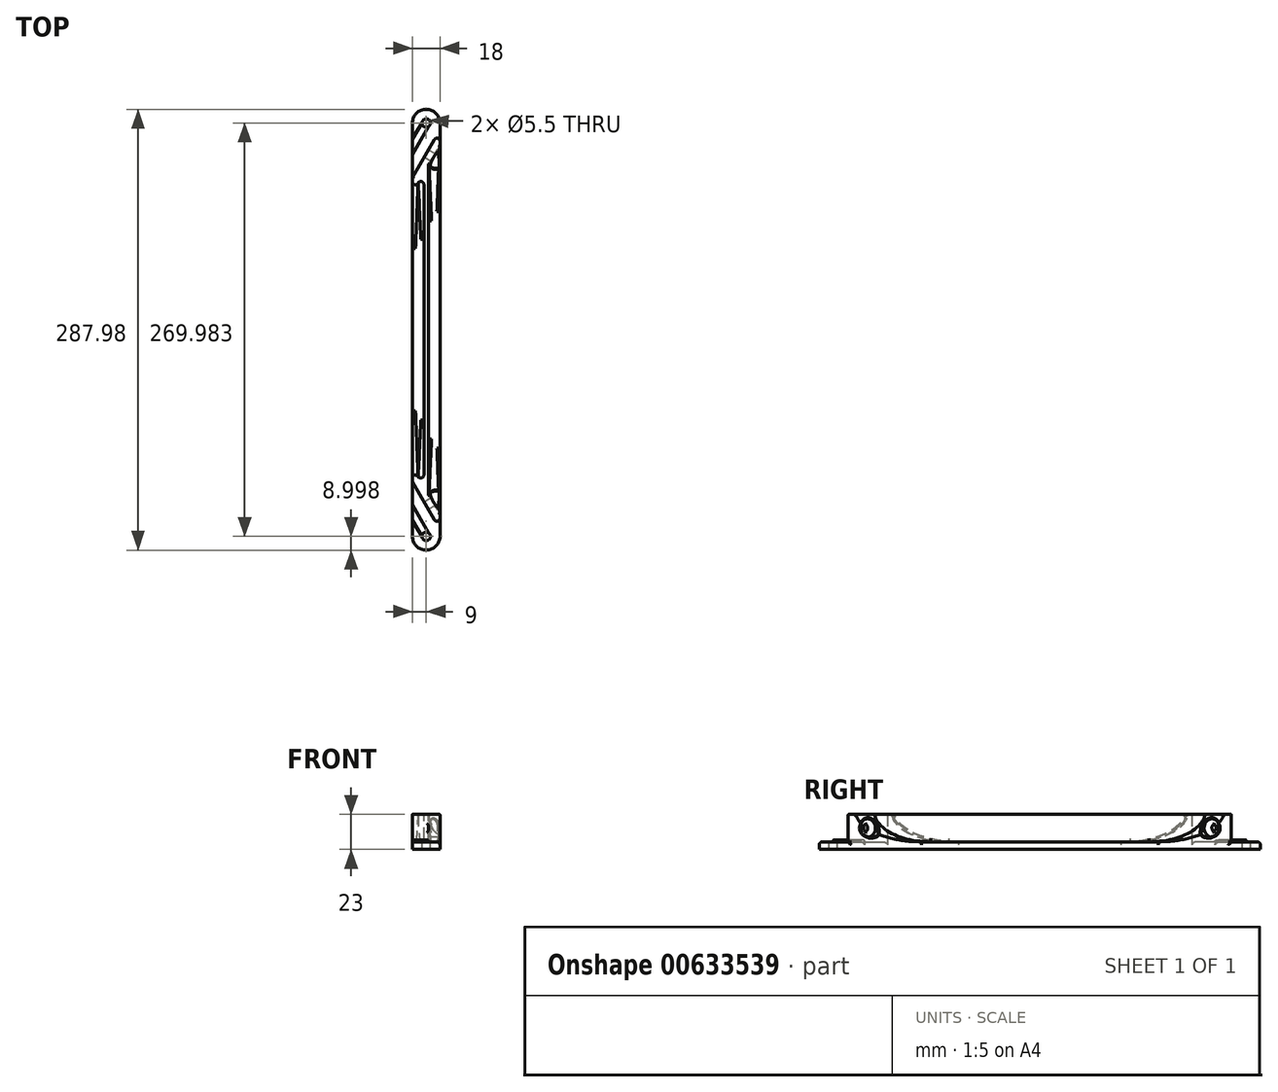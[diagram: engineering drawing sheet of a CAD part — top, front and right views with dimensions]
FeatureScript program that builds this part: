
annotation { "Feature Type Name" : "Feature", "Feature Type Description" : "" }
export const myFeature = defineFeature(function(context is Context, id is Id, definition is map)
    precondition{}
    {
        {
            var Q0;
            Q0=qCreatedBy(makeId("Top.planeOp"),FACE);
            var sketch = newSketch(context, id + "F0", { "sketchPlane" : qUnion([Q0])});
            skLineSegment(sketch, "E0.top", {"start": v(9, 135) * mm, "end": v(-9, 135) * mm, "construction": true});
            skPoint(sketch, "E0.middle", {"position": v(0, 0) * mm});
            skArc(sketch, "E1", {"start": v(-9, 135) * mm, "mid": v(0, 144) * mm, "end": v(9, 135) * mm});
            skCircle(sketch, "E2", {"center": v(0, 135) * mm, "radius": 2.75 * mm});
            skCircle(sketch, "E3", {"center": v(0, 135) * mm, "radius": 2.5 * mm, "construction": true});
            skLineSegment(sketch, "E4", {"start": v(-9.23, 124) * mm, "end": v(2.16, 143.73) * mm});
            skLineSegment(sketch, "E5", {"start": v(-9.23, 114) * mm, "end": v(6.49, 141.23) * mm});
            skCircle(sketch, "E6", {"center": v(0, 135) * mm, "radius": 15 * mm, "construction": true});
            skLineSegment(sketch, "E7.MirrorCS", {"start": v(9, 135) * mm, "end": v(9, 0) * mm});
            skLineSegment(sketch, "E8.MirrorCS", {"start": v(-9, 135) * mm, "end": v(-9, 0) * mm});
            skLineSegment(sketch, "E9", {"start": v(9, 130.58) * mm, "end": v(-9, 99.4) * mm});
            skLineSegment(sketch, "E10", {"start": v(9, 120.58) * mm, "end": v(-9, 89.4) * mm});
            skLineSegment(sketch, "E11", {"start": v(-1.5, 102.4) * mm, "end": v(-1.5, 0) * mm});
            skCircle(sketch, "E12", {"center": v(0, 0) * mm, "radius": 1.5 * mm, "construction": true});
            skLineSegment(sketch, "E13", {"start": v(1.5, 107.59) * mm, "end": v(1.5, 0) * mm});
            skLineSegment(sketch, "E14", {"start": v(-9, 0) * mm, "end": v(9, 0) * mm});
            skCircle(sketch, "E15", {"center": v(1.5, 0) * mm, "radius": 150 * mm, "construction": true});
            skSolve(sketch);
        }
        {
            var Q0;
            Q0=qSketchRegion(id+"F0",true);
            var Q1;
            {var subQ0=sQuery(id+"F0.wireOp",EDGE,"E11");Q1=makeQuery(id+"F0.imprint","IMPRINT",FACE,{"disambiguationData":[TD([[makeQuery(id+"F0.imprint","IMPRINT",EDGE,{"derivedFrom":subQ0}),1.0]])]});}
            extrude(context, id + "F1", {"entities" : qUnion([Q0, Q1]), "oppositeDirection" : true, "depth" : 5 * mm, "offsetDistance" : 25 * mm});
        }
        {
            var Q0;
            {var subQ0=sQuery(id+"F0.wireOp",EDGE,"E4");var subQ1=sQuery(id+"F0.wireOp",EDGE,"E2");var subQ2=makeQuery(id+"F0.imprint","INTERSECT",VERTEX,{"disambiguationData":[OD(0.0)],"derivedFrom":[subQ1,subQ0]});Q0=makeQuery(id+"F0.imprint","IMPRINT",FACE,{"disambiguationData":[TD([[makeQuery(id+"F0.imprint","IMPRINT",EDGE,{"disambiguationData":[TD([[subQ2,-1.0]])],"derivedFrom":subQ1}),-1.0]])]});}
            var Q1;
            {var subQ0=sQuery(id+"F0.wireOp",EDGE,"E4");var subQ1=sQuery(id+"F0.wireOp",EDGE,"E1");var subQ2=makeQuery(id+"F0.imprint","INTERSECT",VERTEX,{"derivedFrom":[subQ1,subQ0]});Q1=makeQuery(id+"F0.imprint","IMPRINT",FACE,{"disambiguationData":[TD([[makeQuery(id+"F0.imprint","IMPRINT",EDGE,{"disambiguationData":[TD([[subQ2,-1.0]])],"derivedFrom":subQ1}),-1.0]])]});}
            var Q2;
            {var subQ0=sQuery(id+"F0.wireOp",EDGE,"3b4f7be5-a3c5-4cc3-b924-c977956cb13f3.MirrorCS");var subQ1=sQuery(id+"F0.wireOp",EDGE,"3b4f7be5-a3c5-4cc3-b924-c977956cb13f0.MirrorC");var subQ2=makeQuery(id+"F0.imprint","INTERSECT",VERTEX,{"disambiguationData":[OD(0.0)],"derivedFrom":[subQ1,subQ0]});Q2=makeQuery(id+"F0.imprint","IMPRINT",FACE,{"disambiguationData":[TD([[makeQuery(id+"F0.imprint","IMPRINT",EDGE,{"disambiguationData":[TD([[subQ2,-1.0]])],"derivedFrom":subQ1}),1.0]])]});}
            var Q3;
            {var subQ0=sQuery(id+"F0.wireOp",EDGE,"3b4f7be5-a3c5-4cc3-b924-c977956cb13f3.MirrorCS");var subQ1=sQuery(id+"F0.wireOp",EDGE,"3b4f7be5-a3c5-4cc3-b924-c977956cb13f0.MirrorC");var subQ2=makeQuery(id+"F0.imprint","INTERSECT",VERTEX,{"disambiguationData":[OD(1.0)],"derivedFrom":[subQ1,subQ0]});Q3=makeQuery(id+"F0.imprint","IMPRINT",FACE,{"disambiguationData":[TD([[makeQuery(id+"F0.imprint","IMPRINT",EDGE,{"disambiguationData":[TD([[subQ2,1.0]])],"derivedFrom":subQ1}),1.0]])]});}
            extrude(context, id + "F2", {"entities" : qUnion([Q0, Q1, Q2, Q3]), "operationType" : NewBodyOperationType.ADD, "depth" : 1.2 * mm, "offsetDistance" : 25 * mm});
        }
        {
            var Q0;
            {var subQ0=sQuery(id+"F0.wireOp",EDGE,"E9");Q0=makeQuery(id+"F0.imprint","IMPRINT",FACE,{"disambiguationData":[TD([[makeQuery(id+"F0.imprint","IMPRINT",EDGE,{"derivedFrom":subQ0}),1.0]])]});}
            var Q1;
            {var subQ0=sQuery(id+"F0.wireOp",EDGE,"52fd9cd9-2778-4df9-a2e4-210ae1353c010.MirrorCS");Q1=makeQuery(id+"F0.imprint","IMPRINT",FACE,{"disambiguationData":[TD([[makeQuery(id+"F0.imprint","IMPRINT",EDGE,{"derivedFrom":subQ0}),-1.0]])]});}
            var Q2;
            {var subQ0=sQuery(id+"F0.wireOp",EDGE,"E11");Q2=makeQuery(id+"F0.imprint","IMPRINT",FACE,{"disambiguationData":[TD([[makeQuery(id+"F0.imprint","IMPRINT",EDGE,{"derivedFrom":subQ0}),1.0]])]});}
            extrude(context, id + "F3", {"entities" : qUnion([Q0, Q1, Q2]), "operationType" : NewBodyOperationType.ADD, "depth" : 18 * mm, "offsetDistance" : 25 * mm});
        }
        {
            var Q0;
            {var subQ0=sQuery(id+"F0.wireOp",EDGE,"E10");Q0=makeQuery(id+"F3.opExtrude","CAP_EDGE",EDGE,{"disambiguationData":[OSD([subQ0]),TDD([makeQuery(id+"F0.imprint","IMPRINT",EDGE,{"disambiguationData":[TD([[makeQuery(id+"F0.imprint","INTERSECT",VERTEX,{"derivedFrom":[sQuery(id+"F0.wireOp",EDGE,"E8.MirrorCS"),subQ0]}),1.0]])],"derivedFrom":subQ0})])],"isStart":true});}
            var Q1;
            {var subQ0=sQuery(id+"F0.wireOp",EDGE,"E10");Q1=makeQuery(id+"F3.opExtrude","CAP_EDGE",EDGE,{"disambiguationData":[OSD([subQ0]),TDD([makeQuery(id+"F0.imprint","IMPRINT",EDGE,{"disambiguationData":[TD([[makeQuery(id+"F0.imprint","INTERSECT",VERTEX,{"derivedFrom":[sQuery(id+"F0.wireOp",EDGE,"E7.MirrorCS"),subQ0]}),-1.0]])],"derivedFrom":subQ0})])],"isStart":true});}
            fillet(context, id + "F4", {"entities" : qUnion([Q0, Q1]), "radius" : 20 * mm, "tangentPropagation" : true, "allowEdgeOverflow" : false});
        }
        {
            var Q0;
            Q0=makeQuery(id+"F3.opExtrude","SWEPT_FACE",FACE,{"disambiguationData":[OSD([sQuery(id+"F0.wireOp",EDGE,"E9")])]});
            var sketch = newSketch(context, id + "F5", { "sketchPlane" : qUnion([Q0])});
            skCircle(sketch, "E16", {"center": v(-99.59, 9) * mm, "radius": 2.75 * mm});
            skCircle(sketch, "E17", {"center": v(-99.59, 9) * mm, "radius": 6 * mm});
            skSolve(sketch);
        }
        {
            var Q0;
            Q0=makeQuery(id+"F5.imprint","IMPRINT",FACE,{"disambiguationData":[TD([[makeQuery(id+"F5.imprint","IMPRINT",EDGE,{"derivedFrom":sQuery(id+"F5.wireOp",EDGE,"E16")}),-1.0]])]});
            var Q1;
            Q1=makeQuery(id+"F5.imprint","IMPRINT",FACE,{"disambiguationData":[TD([[makeQuery(id+"F5.imprint","IMPRINT",EDGE,{"derivedFrom":sQuery(id+"F5.wireOp",EDGE,"E16")}),1.0]])]});
            extrude(context, id + "F6", {"entities" : qUnion([Q0, Q1]), "operationType" : NewBodyOperationType.REMOVE, "oppositeDirection" : true, "depth" : 25 * mm, "offsetDistance" : 25 * mm});
        }
        {
            var Q0;
            Q0=makeQuery(id+"F5.imprint","IMPRINT",FACE,{"disambiguationData":[TD([[makeQuery(id+"F5.imprint","IMPRINT",EDGE,{"derivedFrom":sQuery(id+"F5.wireOp",EDGE,"E16")}),-1.0]])]});
            extrude(context, id + "F7", {"entities" : qUnion([Q0]), "operationType" : NewBodyOperationType.ADD, "oppositeDirection" : true, "depth" : 5 * mm, "offsetDistance" : 25 * mm});
        }
        {
            var Q0;
            {var subQ0=sQuery(id+"F0.wireOp",EDGE,"E8.MirrorCS");var subQ1=sQuery(id+"F0.wireOp",EDGE,"E10");Q0=makeQuery(id+"F4.opFillet","BLEND_EDGE",EDGE,{"blendedFrom":[makeQuery(id+"F3.opExtrude","CAP_EDGE",EDGE,{"disambiguationData":[OSD([subQ1]),TDD([makeQuery(id+"F0.imprint","IMPRINT",EDGE,{"disambiguationData":[TD([[makeQuery(id+"F0.imprint","INTERSECT",VERTEX,{"derivedFrom":[subQ0,subQ1]}),1.0]])],"derivedFrom":subQ1})])],"isStart":true}),makeQuery(id+"F3.boolean.opBoolean","MERGE",FACE,{"derivedFrom":[makeQuery(id+"F2.boolean.opBoolean","MERGE",FACE,{"derivedFrom":[makeQuery(id+"F1.opExtrude","SWEPT_FACE",FACE,{"disambiguationData":[OSD([subQ0])]}),makeQuery(id+"F2.opExtrude","SWEPT_FACE",FACE,{"disambiguationData":[OSD([subQ0])]})]}),makeQuery(id+"F3.opExtrude","SWEPT_FACE",FACE,{"disambiguationData":[OSD([subQ0])]})]})],"blendedInto":[makeQuery(id+"F3.boolean.opBoolean","MERGE",FACE,{"derivedFrom":[makeQuery(id+"F2.boolean.opBoolean","MERGE",FACE,{"derivedFrom":[makeQuery(id+"F1.opExtrude","SWEPT_FACE",FACE,{"disambiguationData":[OSD([subQ0])]}),makeQuery(id+"F2.opExtrude","SWEPT_FACE",FACE,{"disambiguationData":[OSD([subQ0])]})]}),makeQuery(id+"F3.opExtrude","SWEPT_FACE",FACE,{"disambiguationData":[OSD([subQ0])]})]})]});}
            var Q1;
            Q1=makeQuery(id+"F3.opExtrude","SWEPT_EDGE",EDGE,{"disambiguationData":[OSD([sQuery(id+"F0.wireOp",EDGE,"E7.MirrorCS"),sQuery(id+"F0.wireOp",EDGE,"E9")])]});
            var Q2;
            {var subQ0=sQuery(id+"F0.wireOp",EDGE,"E13");var subQ1=sQuery(id+"F0.wireOp",EDGE,"E10");Q2=makeQuery(id+"F4.opFillet","BLEND_EDGE",EDGE,{"blendedFrom":[makeQuery(id+"F3.opExtrude","CAP_EDGE",EDGE,{"disambiguationData":[OSD([subQ1]),TDD([makeQuery(id+"F0.imprint","IMPRINT",EDGE,{"disambiguationData":[TD([[makeQuery(id+"F0.imprint","INTERSECT",VERTEX,{"derivedFrom":[sQuery(id+"F0.wireOp",EDGE,"E7.MirrorCS"),subQ1]}),-1.0]])],"derivedFrom":subQ1})])],"isStart":true}),makeQuery(id+"F3.opExtrude","SWEPT_FACE",FACE,{"disambiguationData":[OSD([subQ0])]})],"blendedInto":[makeQuery(id+"F3.opExtrude","SWEPT_FACE",FACE,{"disambiguationData":[OSD([subQ0])]})]});}
            var Q3;
            Q3=makeQuery(id+"F3.opExtrude","CAP_EDGE",EDGE,{"disambiguationData":[OSD([sQuery(id+"F0.wireOp",EDGE,"E11")])],"isStart":true});
            var Q4;
            {var subQ0=sQuery(id+"F0.wireOp",EDGE,"E8.MirrorCS");var subQ6=sQuery(id+"F0.wireOp",EDGE,"E14");Q4=makeQuery(id+"F3.boolean.opBoolean","SPLIT",EDGE,{"disambiguationData":[TD([makeQuery(id+"F3.opExtrude","SWEPT_FACE",FACE,{"disambiguationData":[OSD([sQuery(id+"F0.wireOp",EDGE,"E9")])]})])],"derivedFrom":makeQuery(id+"F2.boolean.opBoolean","SPLIT",EDGE,{"disambiguationData":[TD([makeQuery(id+"F1.opExtrude","SWEPT_FACE",FACE,{"disambiguationData":[OSD([subQ6])]})])],"derivedFrom":makeQuery(id+"F1.opExtrude","CAP_EDGE",EDGE,{"disambiguationData":[OSD([subQ0])],"isStart":true})})});}
            var Q5;
            {var subQ0=sQuery(id+"F0.wireOp",EDGE,"E1");var subQ1=sQuery(id+"F0.wireOp",EDGE,"E8.MirrorCS");Q5=makeQuery(id+"F2.boolean.opBoolean","SPLIT",EDGE,{"disambiguationData":[TD([makeQuery(id+"F1.opExtrude","SWEPT_FACE",FACE,{"disambiguationData":[OSD([subQ0])]})])],"derivedFrom":makeQuery(id+"F1.opExtrude","CAP_EDGE",EDGE,{"disambiguationData":[OSD([subQ1])],"isStart":true})});}
            var Q6;
            {var subQ0=sQuery(id+"F0.wireOp",EDGE,"E7.MirrorCS");var subQ1=sQuery(id+"F0.wireOp",EDGE,"E1");Q6=makeQuery(id+"F2.boolean.opBoolean","SPLIT",EDGE,{"disambiguationData":[TD([makeQuery(id+"F1.opExtrude","SWEPT_FACE",FACE,{"disambiguationData":[OSD([subQ0])]})])],"derivedFrom":makeQuery(id+"F1.opExtrude","CAP_EDGE",EDGE,{"disambiguationData":[OSD([subQ1])],"isStart":true})});}
            var Q7;
            {var subQ0=sQuery(id+"F0.wireOp",EDGE,"E7.MirrorCS");var subQ1=sQuery(id+"F0.wireOp",EDGE,"E14");Q7=makeQuery(id+"F3.boolean.opBoolean","SPLIT",EDGE,{"disambiguationData":[TD([makeQuery(id+"F1.opExtrude","SWEPT_FACE",FACE,{"disambiguationData":[OSD([subQ1])]})])],"derivedFrom":makeQuery(id+"F1.opExtrude","CAP_EDGE",EDGE,{"disambiguationData":[OSD([subQ0])],"isStart":true})});}
            var Q8;
            {var subQ0=sQuery(id+"F0.wireOp",EDGE,"E10");var subQ1=sQuery(id+"F0.wireOp",EDGE,"E7.MirrorCS");var subQ2=sQuery(id+"F0.wireOp",EDGE,"E13");var subQ3=makeQuery(id+"F3.opExtrude","CAP_EDGE",EDGE,{"disambiguationData":[OSD([subQ0]),TDD([makeQuery(id+"F0.imprint","IMPRINT",EDGE,{"disambiguationData":[TD([[makeQuery(id+"F0.imprint","INTERSECT",VERTEX,{"derivedFrom":[subQ1,subQ0]}),-1.0]])],"derivedFrom":subQ0})])],"isStart":true});var subQ4=makeQuery(id+"F3.opExtrude","SWEPT_FACE",FACE,{"disambiguationData":[OSD([subQ1])]});var subQ5=makeQuery(id+"F1.opExtrude","SWEPT_FACE",FACE,{"disambiguationData":[OSD([subQ1])]});Q8=makeQuery(id+"F6.boolean.opBoolean","SPLIT",EDGE,{"disambiguationData":[TD([makeQuery(id+"F3.opExtrude","CAP_FACE",FACE,{"disambiguationData":[OSD([subQ1,sQuery(id+"F0.wireOp",EDGE,"E8.MirrorCS"),sQuery(id+"F0.wireOp",EDGE,"E9"),subQ0,sQuery(id+"F0.wireOp",EDGE,"E11"),subQ2,sQuery(id+"F0.wireOp",EDGE,"E14")])],"isStart":false})])],"derivedFrom":makeQuery(id+"F4.opFillet","BLEND_EDGE",EDGE,{"blendedFrom":[subQ3,makeQuery(id+"F3.boolean.opBoolean","MERGE",FACE,{"derivedFrom":[subQ5,subQ4]})],"blendedInto":[makeQuery(id+"F3.boolean.opBoolean","MERGE",FACE,{"derivedFrom":[subQ5,subQ4]})]})});}
            fillet(context, id + "F8", {"entities" : qUnion([Q0, Q1, Q2, Q3, Q4, Q5, Q6, Q7, Q8]), "radius" : 2 * mm, "tangentPropagation" : true, "allowEdgeOverflow" : false});
        }
        {
            var Q0;
            Q0=makeQuery(id+"F2.opExtrude","CAP_FACE",FACE,{"disambiguationData":[OSD([sQuery(id+"F0.wireOp",EDGE,"E2"),sQuery(id+"F0.wireOp",EDGE,"E4"),sQuery(id+"F0.wireOp",EDGE,"E5"),sQuery(id+"F0.wireOp",EDGE,"E8.MirrorCS")])],"isStart":false});
            var Q1;
            Q1=makeQuery(id+"F2.opExtrude","CAP_FACE",FACE,{"disambiguationData":[OSD([sQuery(id+"F0.wireOp",EDGE,"E1"),sQuery(id+"F0.wireOp",EDGE,"E2"),sQuery(id+"F0.wireOp",EDGE,"E4"),sQuery(id+"F0.wireOp",EDGE,"E5")])],"isStart":false});
            var Q2;
            {var subQ0=sQuery(id+"F0.wireOp",EDGE,"E4");Q2=makeQuery(id+"F2.opExtrude","CAP_EDGE",EDGE,{"disambiguationData":[OSD([subQ0]),TDD([makeQuery(id+"F0.imprint","IMPRINT",EDGE,{"disambiguationData":[TD([[makeQuery(id+"F0.imprint","INTERSECT",VERTEX,{"derivedFrom":[sQuery(id+"F0.wireOp",EDGE,"E1"),subQ0]}),1.0]])],"derivedFrom":subQ0})])],"isStart":true});}
            var Q3;
            {var subQ0=sQuery(id+"F0.wireOp",EDGE,"E5");Q3=makeQuery(id+"F2.opExtrude","CAP_EDGE",EDGE,{"disambiguationData":[OSD([subQ0]),TDD([makeQuery(id+"F0.imprint","IMPRINT",EDGE,{"disambiguationData":[TD([[makeQuery(id+"F0.imprint","INTERSECT",VERTEX,{"derivedFrom":[subQ0,sQuery(id+"F0.wireOp",EDGE,"E8.MirrorCS")]}),-1.0]])],"derivedFrom":subQ0})])],"isStart":true});}
            var Q4;
            Q4=makeQuery(id+"F3.opExtrude","CAP_EDGE",EDGE,{"disambiguationData":[OSD([sQuery(id+"F0.wireOp",EDGE,"E9")])],"isStart":true});
            var Q5;
            {var subQ0=sQuery(id+"F0.wireOp",EDGE,"E9");var subQ1=sQuery(id+"F0.wireOp",EDGE,"E7.MirrorCS");Q5=makeQuery(id+"F8.opFillet","BLEND_EDGE",EDGE,{"blendedFrom":[makeQuery(id+"F3.opExtrude","SWEPT_EDGE",EDGE,{"disambiguationData":[OSD([subQ1,subQ0])]}),makeQuery(id+"F3.opExtrude","CAP_FACE",FACE,{"disambiguationData":[OSD([subQ1,sQuery(id+"F0.wireOp",EDGE,"E8.MirrorCS"),subQ0,sQuery(id+"F0.wireOp",EDGE,"E10"),sQuery(id+"F0.wireOp",EDGE,"E11"),sQuery(id+"F0.wireOp",EDGE,"E13"),sQuery(id+"F0.wireOp",EDGE,"E14")])],"isStart":false})],"blendedInto":[makeQuery(id+"F3.opExtrude","CAP_FACE",FACE,{"disambiguationData":[OSD([subQ1,sQuery(id+"F0.wireOp",EDGE,"E8.MirrorCS"),subQ0,sQuery(id+"F0.wireOp",EDGE,"E10"),sQuery(id+"F0.wireOp",EDGE,"E11"),sQuery(id+"F0.wireOp",EDGE,"E13"),sQuery(id+"F0.wireOp",EDGE,"E14")])],"isStart":false})]});}
            var Q6;
            {var subQ0=sQuery(id+"F0.wireOp",EDGE,"E11");var subQ1=sQuery(id+"F0.wireOp",EDGE,"E10");var subQ2=sQuery(id+"F0.wireOp",EDGE,"E8.MirrorCS");Q6=makeQuery(id+"F8.opFillet","BLEND_EDGE",EDGE,{"blendedFrom":[makeQuery(id+"F4.opFillet","BLEND_EDGE",EDGE,{"blendedFrom":[makeQuery(id+"F3.opExtrude","CAP_EDGE",EDGE,{"disambiguationData":[OSD([subQ1]),TDD([makeQuery(id+"F0.imprint","IMPRINT",EDGE,{"disambiguationData":[TD([[makeQuery(id+"F0.imprint","INTERSECT",VERTEX,{"derivedFrom":[subQ2,subQ1]}),1.0]])],"derivedFrom":subQ1})])],"isStart":true}),makeQuery(id+"F3.boolean.opBoolean","MERGE",FACE,{"derivedFrom":[makeQuery(id+"F2.boolean.opBoolean","MERGE",FACE,{"derivedFrom":[makeQuery(id+"F1.opExtrude","SWEPT_FACE",FACE,{"disambiguationData":[OSD([subQ2])]}),makeQuery(id+"F2.opExtrude","SWEPT_FACE",FACE,{"disambiguationData":[OSD([subQ2])]})]}),makeQuery(id+"F3.opExtrude","SWEPT_FACE",FACE,{"disambiguationData":[OSD([subQ2])]})]})],"blendedInto":[makeQuery(id+"F3.boolean.opBoolean","MERGE",FACE,{"derivedFrom":[makeQuery(id+"F2.boolean.opBoolean","MERGE",FACE,{"derivedFrom":[makeQuery(id+"F1.opExtrude","SWEPT_FACE",FACE,{"disambiguationData":[OSD([subQ2])]}),makeQuery(id+"F2.opExtrude","SWEPT_FACE",FACE,{"disambiguationData":[OSD([subQ2])]})]}),makeQuery(id+"F3.opExtrude","SWEPT_FACE",FACE,{"disambiguationData":[OSD([subQ2])]})]})]}),makeQuery(id+"F3.opExtrude","CAP_FACE",FACE,{"disambiguationData":[OSD([sQuery(id+"F0.wireOp",EDGE,"E7.MirrorCS"),subQ2,sQuery(id+"F0.wireOp",EDGE,"E9"),subQ1,subQ0,sQuery(id+"F0.wireOp",EDGE,"E13"),sQuery(id+"F0.wireOp",EDGE,"E14")])],"isStart":false})],"blendedInto":[makeQuery(id+"F3.opExtrude","CAP_FACE",FACE,{"disambiguationData":[OSD([sQuery(id+"F0.wireOp",EDGE,"E7.MirrorCS"),subQ2,sQuery(id+"F0.wireOp",EDGE,"E9"),subQ1,subQ0,sQuery(id+"F0.wireOp",EDGE,"E13"),sQuery(id+"F0.wireOp",EDGE,"E14")])],"isStart":false})]});}
            var Q7;
            Q7=makeQuery(id+"FkMoG665bWaejhP_1.boolean.opBoolean","COPY",EDGE,{"derivedFrom":makeQuery(id+"FkMoG665bWaejhP_1.opExtrude","TWEAK_EDGE",EDGE,{"derivedFrom":[makeQuery(id+"F3.opExtrude","SWEPT_FACE",FACE,{"disambiguationData":[OSD([sQuery(id+"F0.wireOp",EDGE,"E13")])]}),makeQuery(id+"FedeHjCdRSWNe7W_1.imprint","IMPRINT",EDGE,{"derivedFrom":sQuery(id+"FedeHjCdRSWNe7W_1.wireOp",EDGE,"edfF8cXi-Lyam-Ilsb-Idl7-8AkXt3HHKT67")})]})});
            var Q8;
            {var subQ0=sQuery(id+"F0.wireOp",EDGE,"E11");var subQ1=sQuery(id+"F0.wireOp",EDGE,"E10");Q8=makeQuery(id+"F8.opFillet","BLEND_EDGE",EDGE,{"blendedFrom":[makeQuery(id+"F4.opFillet","BLEND_EDGE",EDGE,{"blendedFrom":[makeQuery(id+"F3.opExtrude","CAP_EDGE",EDGE,{"disambiguationData":[OSD([subQ1]),TDD([makeQuery(id+"F0.imprint","IMPRINT",EDGE,{"disambiguationData":[TD([[makeQuery(id+"F0.imprint","INTERSECT",VERTEX,{"derivedFrom":[sQuery(id+"F0.wireOp",EDGE,"E8.MirrorCS"),subQ1]}),1.0]])],"derivedFrom":subQ1})])],"isStart":true}),makeQuery(id+"F3.opExtrude","SWEPT_FACE",FACE,{"disambiguationData":[OSD([subQ0])]})],"blendedInto":[makeQuery(id+"F3.opExtrude","SWEPT_FACE",FACE,{"disambiguationData":[OSD([subQ0])]})]}),makeQuery(id+"FkMoG665bWaejhP_1.boolean.opBoolean","COPY",FACE,{"derivedFrom":makeQuery(id+"FkMoG665bWaejhP_1.opExtrude","SWEPT_FACE",FACE,{"disambiguationData":[OSD([sQuery(id+"FedeHjCdRSWNe7W_1.wireOp",EDGE,"edfF8cXi-Lyam-Ilsb-Idl7-8AkXt3HHKT67")])]})})],"blendedInto":[makeQuery(id+"FkMoG665bWaejhP_1.boolean.opBoolean","COPY",FACE,{"derivedFrom":makeQuery(id+"FkMoG665bWaejhP_1.opExtrude","SWEPT_FACE",FACE,{"disambiguationData":[OSD([sQuery(id+"FedeHjCdRSWNe7W_1.wireOp",EDGE,"edfF8cXi-Lyam-Ilsb-Idl7-8AkXt3HHKT67")])]})})]});}
            var Q9;
            {var subQ0=sQuery(id+"F0.wireOp",EDGE,"E13");var subQ1=sQuery(id+"F0.wireOp",EDGE,"E10");var subQ2=sQuery(id+"F0.wireOp",EDGE,"E7.MirrorCS");Q9=makeQuery(id+"F4.opFillet","BLEND_EDGE",EDGE,{"blendedFrom":[makeQuery(id+"F3.opExtrude","CAP_EDGE",EDGE,{"disambiguationData":[OSD([subQ1]),TDD([makeQuery(id+"F0.imprint","IMPRINT",EDGE,{"disambiguationData":[TD([[makeQuery(id+"F0.imprint","INTERSECT",VERTEX,{"derivedFrom":[subQ2,subQ1]}),-1.0]])],"derivedFrom":subQ1})])],"isStart":true}),makeQuery(id+"F3.opExtrude","CAP_FACE",FACE,{"disambiguationData":[OSD([subQ2,sQuery(id+"F0.wireOp",EDGE,"E8.MirrorCS"),sQuery(id+"F0.wireOp",EDGE,"E9"),subQ1,sQuery(id+"F0.wireOp",EDGE,"E11"),subQ0,sQuery(id+"F0.wireOp",EDGE,"E14")])],"isStart":false})],"blendedInto":[makeQuery(id+"F3.opExtrude","CAP_FACE",FACE,{"disambiguationData":[OSD([subQ2,sQuery(id+"F0.wireOp",EDGE,"E8.MirrorCS"),sQuery(id+"F0.wireOp",EDGE,"E9"),subQ1,sQuery(id+"F0.wireOp",EDGE,"E11"),subQ0,sQuery(id+"F0.wireOp",EDGE,"E14")])],"isStart":false})]});}
            var Q10;
            {var subQ0=sQuery(id+"F0.wireOp",EDGE,"E7.MirrorCS");Q10=makeQuery(id+"F6.boolean.opBoolean","INTERSECT",EDGE,{"derivedFrom":[makeQuery(id+"F3.boolean.opBoolean","MERGE",FACE,{"derivedFrom":[makeQuery(id+"F1.opExtrude","SWEPT_FACE",FACE,{"disambiguationData":[OSD([subQ0])]}),makeQuery(id+"F3.opExtrude","SWEPT_FACE",FACE,{"disambiguationData":[OSD([subQ0])]})]}),makeQuery(id+"F6.opExtrude","SWEPT_FACE",FACE,{"disambiguationData":[OSD([sQuery(id+"F5.wireOp",EDGE,"E17")])]})]});}
            var Q11;
            Q11=makeQuery(id+"F7.opExtrude","CAP_EDGE",EDGE,{"disambiguationData":[OSD([sQuery(id+"F5.wireOp",EDGE,"E16")])],"isStart":false});
            var Q12;
            Q12=makeQuery(id+"F7.opExtrude","CAP_EDGE",EDGE,{"disambiguationData":[OSD([sQuery(id+"F5.wireOp",EDGE,"E16")])],"isStart":true});
            fillet(context, id + "F9", {"entities" : qUnion([Q0, Q1, Q2, Q3, Q4, Q5, Q6, Q7, Q8, Q9, Q10, Q11, Q12]), "radius" : 0.6 * mm, "tangentPropagation" : true, "allowEdgeOverflow" : false});
        }
        {
            var Q0;
            Q0=makeQuery(id+"F1.opExtrude","SWEPT_BODY",BODY,{"disambiguationData":[OSD([sQuery(id+"F0.wireOp",EDGE,"E1"),sQuery(id+"F0.wireOp",EDGE,"E2"),sQuery(id+"F0.wireOp",EDGE,"E7.MirrorCS"),sQuery(id+"F0.wireOp",EDGE,"E8.MirrorCS"),sQuery(id+"F0.wireOp",EDGE,"E14")])]});
            var Q1;
            Q1=qCreatedBy(makeId("Front.planeOp"),FACE);
            mirror(context, id + "F10", {"operationType" : NewBodyOperationType.ADD, "entities" : qUnion([Q0]), "mirrorPlane" : qUnion([Q1])});
        }
    });
